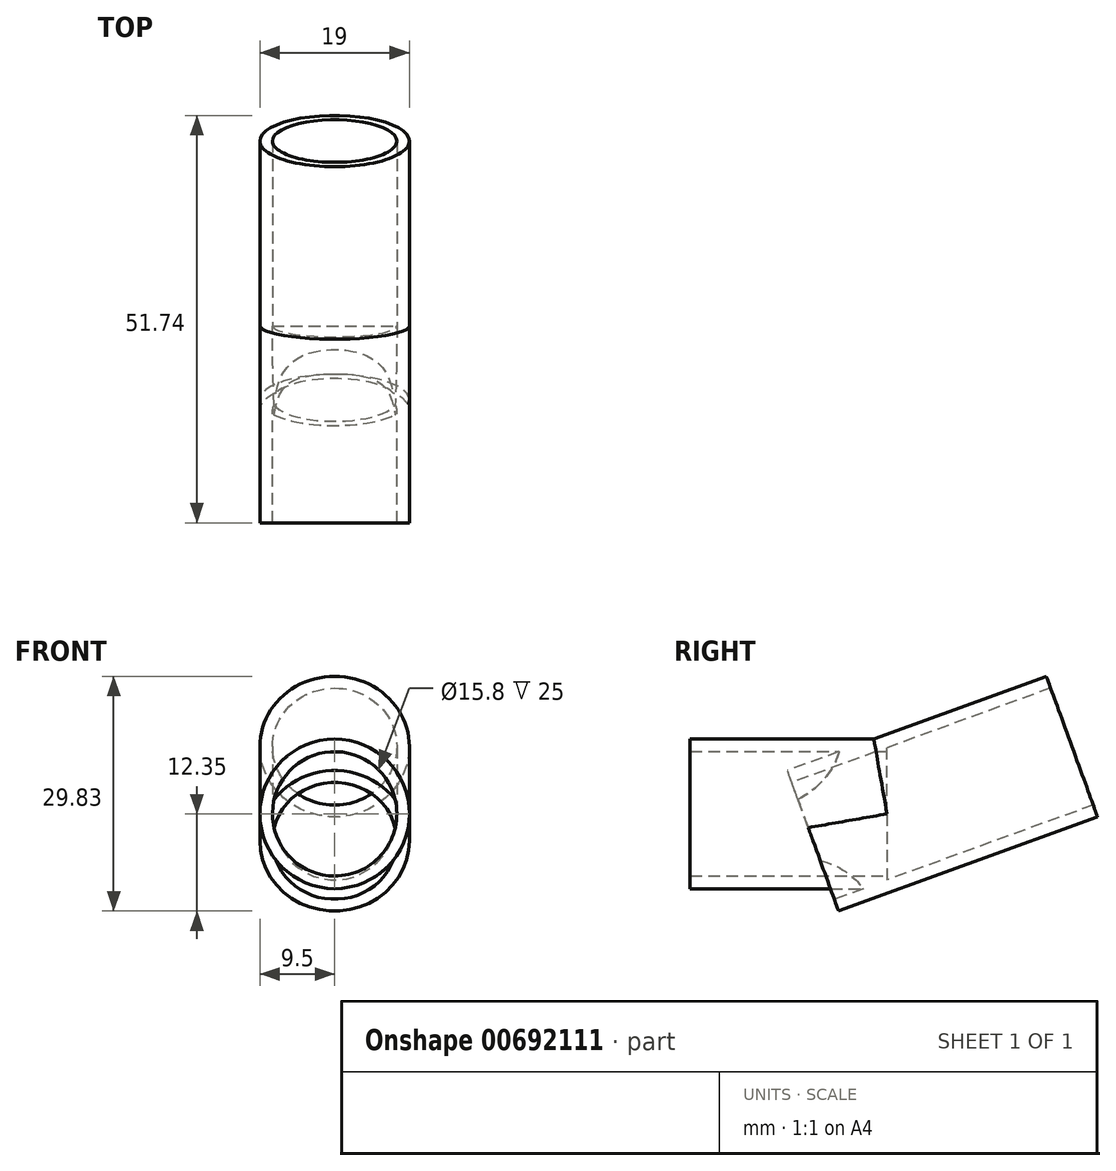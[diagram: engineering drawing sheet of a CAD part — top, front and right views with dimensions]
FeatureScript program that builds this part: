
annotation { "Feature Type Name" : "Feature", "Feature Type Description" : "" }
export const myFeature = defineFeature(function(context is Context, id is Id, definition is map)
    precondition{}
    {
        {
            var Q0;
            Q0=qCreatedBy(makeId("Front.planeOp"),FACE);
            var sketch = newSketch(context, id + "F0", { "sketchPlane" : qUnion([Q0])});
            skCircle(sketch, "E0", {"center": v(0, 0) * mm, "radius": 9.5 * mm});
            skCircle(sketch, "E1", {"center": v(0, 0) * mm, "radius": 7.9 * mm});
            skSolve(sketch);
        }
        {
            var Q0;
            Q0 = qSketchRegion(id + "F0", true);
            extrude(context, id + "F1", {"entities" : qUnion([Q0]), "depth" : 25 * mm, "offsetDistance" : 25 * mm});
        }
        {
            var Q0;
            Q0=qCreatedBy(makeId("Right.planeOp"),FACE);
            var sketch = newSketch(context, id + "F2", { "sketchPlane" : qUnion([Q0])});
            skCircle(sketch, "E2", {"center": v(0, 0) * mm, "radius": 9.5 * mm});
            skCircle(sketch, "E3", {"center": v(0, 0) * mm, "radius": 7.9 * mm});
            skSolve(sketch);
        }
        {
            var Q0;
            Q0=sQuery(id+"F2.wireOp",EDGE,"E2");
            cPlane(context, id + "F3", {"entities" : qUnion([Q0]), "cplaneType" : CPlaneType.LINE_ANGLE, "offset" : 25 * mm, "angle" : 20 * degree, "width" : 150 * mm, "height" : 150 * mm});
        }
        {
            var Q0;
            Q0=qCreatedBy(id+"F3.planeOp",FACE);
            var sketch = newSketch(context, id + "F4", { "sketchPlane" : qUnion([Q0])});
            skCircle(sketch, "E4", {"center": v(0, 0) * mm, "radius": 9.5 * mm});
            skCircle(sketch, "E5", {"center": v(0, 0) * mm, "radius": 7.9 * mm});
            skSolve(sketch);
        }
        {
            var Q0;
            Q0 = qSketchRegion(id + "F4", true);
            extrude(context, id + "F5", {"entities" : qUnion([Q0]), "depth" : 25 * mm, "offsetDistance" : 25 * mm, "hasSecondDirection" : true, "secondDirectionOppositeDirection" : true, "secondDirectionDepth" : 10 * mm});
        }
        {
            var Q0;
            {var subQ0=sQuery(id+"F0.wireOp",EDGE,"E1");var subQ1=sQuery(id+"F4.wireOp",EDGE,"E5");var subQ2=sQuery(id+"F4.wireOp",EDGE,"E4");var subQ3=makeQuery(id+"F5.opExtrude","CAP_FACE",FACE,{"disambiguationData":[OSD([subQ2,subQ1])],"isStart":true});var subQ4=sQuery(id+"F0.wireOp",EDGE,"E0");Q0=makeQuery(id+"F5.boolean.opBoolean","SPLIT",FACE,{"disambiguationData":[TD([makeQuery(id+"F1.opExtrude","SWEPT_FACE",FACE,{"disambiguationData":[OSD([subQ4])]}),makeQuery(id+"F1.opExtrude","CAP_FACE",FACE,{"disambiguationData":[OSD([subQ4,subQ0])],"isStart":true}),makeQuery(id+"F1.opExtrude","SWEPT_FACE",FACE,{"disambiguationData":[OSD([subQ0])]}),makeQuery(id+"F5.opExtrude","SWEPT_FACE",FACE,{"disambiguationData":[OSD([subQ2])]}),subQ3,makeQuery(id+"F5.opExtrude","SWEPT_FACE",FACE,{"disambiguationData":[OSD([subQ1])]})])],"derivedFrom":subQ3});}
            extrude(context, id + "F6", {"entities" : qUnion([Q0]), "operationType" : NewBodyOperationType.ADD, "oppositeDirection" : true, "depth" : 25 * mm, "offsetDistance" : 25 * mm});
        }
    });
